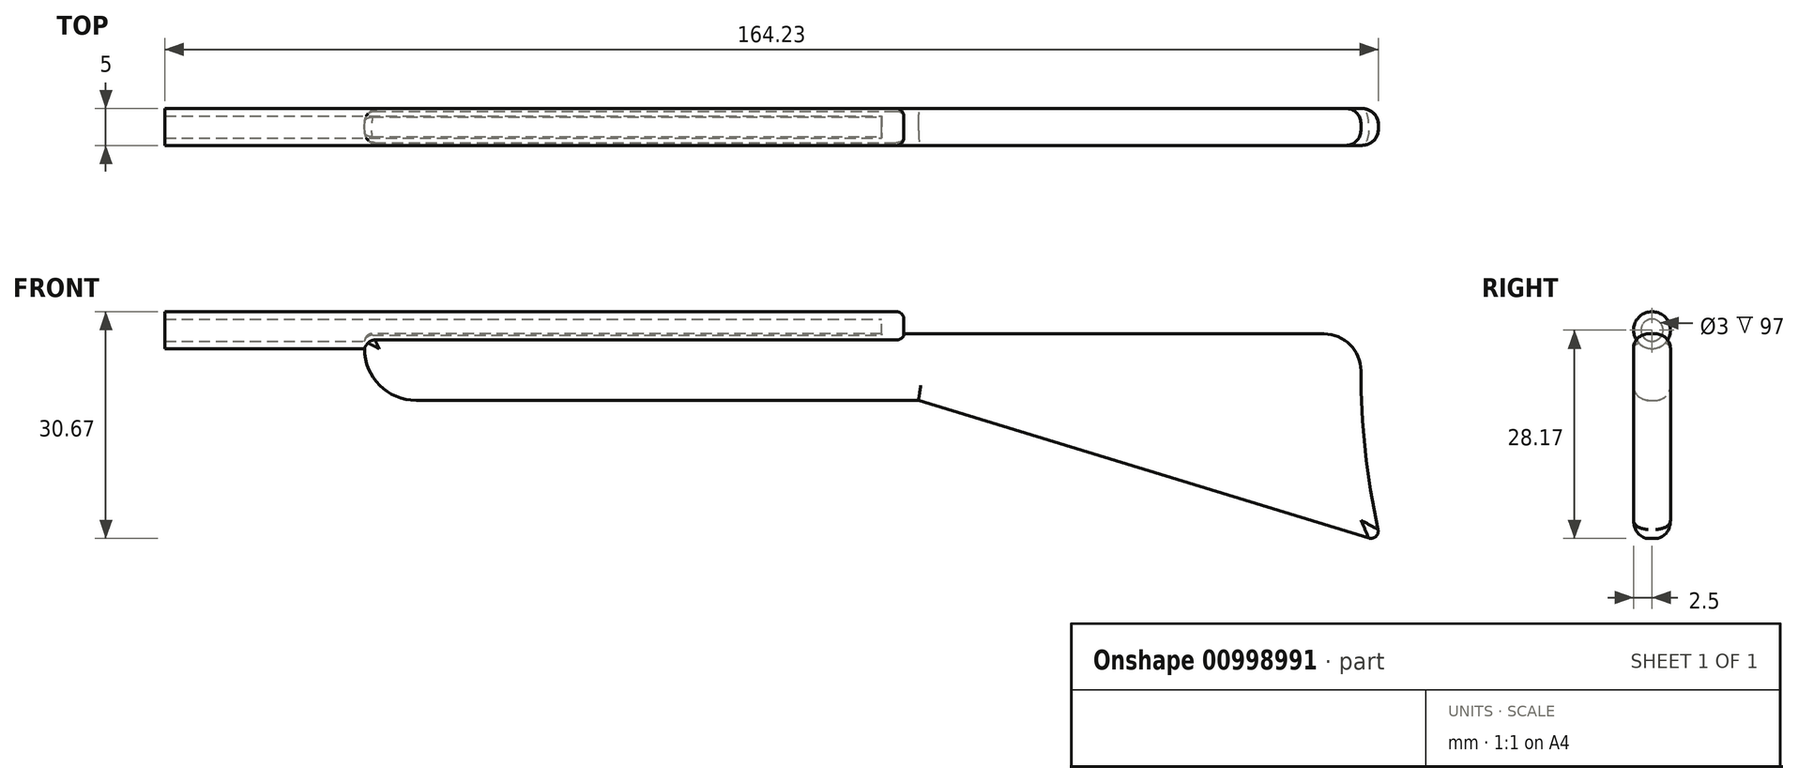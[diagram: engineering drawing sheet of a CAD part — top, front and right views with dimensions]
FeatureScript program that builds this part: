
annotation { "Feature Type Name" : "Feature", "Feature Type Description" : "" }
export const myFeature = defineFeature(function(context is Context, id is Id, definition is map)
    precondition{}
    {
        {
            var Q0;
            Q0=qCreatedBy(makeId("Front.planeOp"),FACE);
            var sketch = newSketch(context, id + "F0", { "sketchPlane" : qUnion([Q0])});
            skLineSegment(sketch, "E0.bottom", {"start": v(-100, 5) * mm, "end": v(0, 5) * mm});
            skLineSegment(sketch, "E0.top", {"start": v(-100, 0) * mm, "end": v(0, 0) * mm});
            skLineSegment(sketch, "E0.left", {"start": v(-100, 5) * mm, "end": v(-100, 0) * mm});
            skLineSegment(sketch, "E0.right", {"start": v(0, 5) * mm, "end": v(0, 0) * mm});
            skArc(sketch, "E1", {"start": v(-73, 0) * mm, "mid": v(-70.95, -4.95) * mm, "end": v(-66, -7) * mm});
            skLineSegment(sketch, "E2", {"start": v(-66, -7) * mm, "end": v(2, -7) * mm});
            skLineSegment(sketch, "E3", {"start": v(2, -7) * mm, "end": v(64.59, -26.14) * mm});
            skArc(sketch, "E4", {"start": v(62, 2) * mm, "mid": v(62.3, -12.16) * mm, "end": v(64.59, -26.14) * mm});
            skPoint(sketch, "E5.endSnap0", {"position": v(0, 2.5) * mm});
            skLineSegment(sketch, "E6", {"start": v(62, 2) * mm, "end": v(-73, 2) * mm});
            skLineSegment(sketch, "E7", {"start": v(-73, 2) * mm, "end": v(-73, 0) * mm});
            skSolve(sketch);
        }
        {
            var Q0;
            Q0=qCreatedBy(makeId("Front.planeOp"),FACE);
            var sketch = newSketch(context, id + "F1", { "sketchPlane" : qUnion([Q0])});
            skArc(sketch, "E8.4", {"start": v(-73, 0) * mm, "mid": v(-70.95, -4.95) * mm, "end": v(-66, -7) * mm});
            skLineSegment(sketch, "E8.5", {"start": v(-66, -7) * mm, "end": v(2, -7) * mm});
            skLineSegment(sketch, "E8.6", {"start": v(2, -7) * mm, "end": v(64.59, -26.14) * mm});
            skArc(sketch, "E8.7", {"start": v(62, 2) * mm, "mid": v(62.3, -12.16) * mm, "end": v(64.59, -26.14) * mm});
            skLineSegment(sketch, "E8.9", {"start": v(62, 2) * mm, "end": v(-73, 2) * mm});
            skLineSegment(sketch, "E8.10", {"start": v(-73, 2) * mm, "end": v(-73, 0) * mm});
            skSolve(sketch);
        }
        {
            var Q0;
            Q0 = qSketchRegion(id + "F1", true);
            extrude(context, id + "F2", {"entities" : qUnion([Q0]), "endBound" : BoundingType.SYMMETRIC, "depth" : 5 * mm, "offsetDistance" : 25 * mm});
        }
        {
            var Q0;
            Q0=makeQuery(id+"F2.opExtrude","CAP_FACE",FACE,{"disambiguationData":[OSD([sQuery(id+"F1.wireOp",EDGE,"E8.4"),sQuery(id+"F1.wireOp",EDGE,"E8.5"),sQuery(id+"F1.wireOp",EDGE,"E8.6"),sQuery(id+"F1.wireOp",EDGE,"E8.7"),sQuery(id+"F1.wireOp",EDGE,"E8.9"),sQuery(id+"F1.wireOp",EDGE,"E8.10")])],"isStart":false});
            var Q1;
            Q1=makeQuery(id+"F2.opExtrude","CAP_FACE",FACE,{"disambiguationData":[OSD([sQuery(id+"F1.wireOp",EDGE,"E8.4"),sQuery(id+"F1.wireOp",EDGE,"E8.5"),sQuery(id+"F1.wireOp",EDGE,"E8.6"),sQuery(id+"F1.wireOp",EDGE,"E8.7"),sQuery(id+"F1.wireOp",EDGE,"E8.9"),sQuery(id+"F1.wireOp",EDGE,"E8.10")])],"isStart":true});
            fillet(context, id + "F3", {"entities" : qUnion([Q0, Q1]), "radius" : 2 * mm, "tangentPropagation" : true, "allowEdgeOverflow" : false});
        }
        {
            var Q0;
            Q0=makeQuery(id+"F2.opExtrude","SWEPT_EDGE",EDGE,{"disambiguationData":[OSD([sQuery(id+"F1.wireOp",EDGE,"E8.7"),sQuery(id+"F1.wireOp",EDGE,"E8.9")])]});
            var Q1;
            Q1=makeQuery(id+"F3.opFillet","BLEND_EDGE",EDGE,{"blendedFrom":[makeQuery(id+"F2.opExtrude","CAP_EDGE",EDGE,{"disambiguationData":[OSD([sQuery(id+"F1.wireOp",EDGE,"E8.7")])],"isStart":false}),makeQuery(id+"F2.opExtrude","CAP_EDGE",EDGE,{"disambiguationData":[OSD([sQuery(id+"F1.wireOp",EDGE,"E8.9")])],"isStart":false})],"blendedInto":[]});
            var Q2;
            Q2=makeQuery(id+"F3.opFillet","BLEND_EDGE",EDGE,{"blendedFrom":[makeQuery(id+"F2.opExtrude","CAP_EDGE",EDGE,{"disambiguationData":[OSD([sQuery(id+"F1.wireOp",EDGE,"E8.7")])],"isStart":true}),makeQuery(id+"F2.opExtrude","CAP_EDGE",EDGE,{"disambiguationData":[OSD([sQuery(id+"F1.wireOp",EDGE,"E8.9")])],"isStart":true})],"blendedInto":[]});
            fillet(context, id + "F4", {"entities" : qUnion([Q0, Q1, Q2]), "radius" : 5 * mm, "tangentPropagation" : true, "allowEdgeOverflow" : false});
        }
        {
            var Q0;
            Q0=makeQuery(id+"F2.opExtrude","SWEPT_EDGE",EDGE,{"disambiguationData":[OSD([sQuery(id+"F1.wireOp",EDGE,"E8.6"),sQuery(id+"F1.wireOp",EDGE,"E8.7")])]});
            var Q1;
            Q1=makeQuery(id+"F3.opFillet","BLEND_EDGE",EDGE,{"blendedFrom":[makeQuery(id+"F2.opExtrude","CAP_EDGE",EDGE,{"disambiguationData":[OSD([sQuery(id+"F1.wireOp",EDGE,"E8.6")])],"isStart":true}),makeQuery(id+"F2.opExtrude","CAP_EDGE",EDGE,{"disambiguationData":[OSD([sQuery(id+"F1.wireOp",EDGE,"E8.7")])],"isStart":true})],"blendedInto":[]});
            var Q2;
            Q2=makeQuery(id+"F3.opFillet","BLEND_EDGE",EDGE,{"blendedFrom":[makeQuery(id+"F2.opExtrude","CAP_EDGE",EDGE,{"disambiguationData":[OSD([sQuery(id+"F1.wireOp",EDGE,"E8.6")])],"isStart":false}),makeQuery(id+"F2.opExtrude","CAP_EDGE",EDGE,{"disambiguationData":[OSD([sQuery(id+"F1.wireOp",EDGE,"E8.7")])],"isStart":false})],"blendedInto":[]});
            var Q3;
            Q3=makeQuery(id+"F3.opFillet","BLEND_EDGE",EDGE,{"blendedFrom":[makeQuery(id+"F2.opExtrude","CAP_EDGE",EDGE,{"disambiguationData":[OSD([sQuery(id+"F1.wireOp",EDGE,"E8.4")])],"isStart":true}),makeQuery(id+"F2.opExtrude","CAP_EDGE",EDGE,{"disambiguationData":[OSD([sQuery(id+"F1.wireOp",EDGE,"E8.10")])],"isStart":true})],"blendedInto":[]});
            var Q4;
            Q4=makeQuery(id+"F2.opExtrude","SWEPT_EDGE",EDGE,{"disambiguationData":[OSD([sQuery(id+"F1.wireOp",EDGE,"E8.4"),sQuery(id+"F1.wireOp",EDGE,"E8.10")])]});
            var Q5;
            Q5=makeQuery(id+"F3.opFillet","BLEND_EDGE",EDGE,{"blendedFrom":[makeQuery(id+"F2.opExtrude","CAP_EDGE",EDGE,{"disambiguationData":[OSD([sQuery(id+"F1.wireOp",EDGE,"E8.4")])],"isStart":false}),makeQuery(id+"F2.opExtrude","CAP_EDGE",EDGE,{"disambiguationData":[OSD([sQuery(id+"F1.wireOp",EDGE,"E8.10")])],"isStart":false})],"blendedInto":[]});
            var Q6;
            Q6=makeQuery(id+"F3.opFillet","BLEND_EDGE",EDGE,{"blendedFrom":[makeQuery(id+"F2.opExtrude","CAP_EDGE",EDGE,{"disambiguationData":[OSD([sQuery(id+"F1.wireOp",EDGE,"E8.9")])],"isStart":true}),makeQuery(id+"F2.opExtrude","CAP_EDGE",EDGE,{"disambiguationData":[OSD([sQuery(id+"F1.wireOp",EDGE,"E8.10")])],"isStart":true})],"blendedInto":[]});
            var Q7;
            Q7=makeQuery(id+"F3.opFillet","BLEND_EDGE",EDGE,{"blendedFrom":[makeQuery(id+"F2.opExtrude","CAP_EDGE",EDGE,{"disambiguationData":[OSD([sQuery(id+"F1.wireOp",EDGE,"E8.9")])],"isStart":false}),makeQuery(id+"F2.opExtrude","CAP_EDGE",EDGE,{"disambiguationData":[OSD([sQuery(id+"F1.wireOp",EDGE,"E8.10")])],"isStart":false})],"blendedInto":[]});
            var Q8;
            Q8=makeQuery(id+"F2.opExtrude","SWEPT_EDGE",EDGE,{"disambiguationData":[OSD([sQuery(id+"F1.wireOp",EDGE,"E8.9"),sQuery(id+"F1.wireOp",EDGE,"E8.10")])]});
            var Q9;
            {var subQ0=sQuery(id+"F1.wireOp",EDGE,"E8.10");Q9=makeQuery(id+"F3.opFillet","BLEND_EDGE",EDGE,{"blendedFrom":[makeQuery(id+"F2.opExtrude","CAP_EDGE",EDGE,{"disambiguationData":[OSD([subQ0])],"isStart":true}),makeQuery(id+"F2.opExtrude","SWEPT_FACE",FACE,{"disambiguationData":[OSD([subQ0])]})],"blendedInto":[makeQuery(id+"F2.opExtrude","SWEPT_FACE",FACE,{"disambiguationData":[OSD([subQ0])]})]});}
            var Q10;
            {var subQ0=sQuery(id+"F1.wireOp",EDGE,"E8.10");Q10=makeQuery(id+"F3.opFillet","BLEND_EDGE",EDGE,{"blendedFrom":[makeQuery(id+"F2.opExtrude","CAP_EDGE",EDGE,{"disambiguationData":[OSD([subQ0])],"isStart":false}),makeQuery(id+"F2.opExtrude","SWEPT_FACE",FACE,{"disambiguationData":[OSD([subQ0])]})],"blendedInto":[makeQuery(id+"F2.opExtrude","SWEPT_FACE",FACE,{"disambiguationData":[OSD([subQ0])]})]});}
            fillet(context, id + "F5", {"entities" : qUnion([Q0, Q1, Q2, Q3, Q4, Q5, Q6, Q7, Q8, Q9, Q10]), "radius" : 1 * mm, "tangentPropagation" : true, "allowEdgeOverflow" : false});
        }
        {
            var Q0;
            Q0=qCreatedBy(makeId("Front.planeOp"),FACE);
            var sketch = newSketch(context, id + "F6", { "sketchPlane" : qUnion([Q0])});
            skLineSegment(sketch, "E9.0", {"start": v(-100, 5) * mm, "end": v(0, 5) * mm});
            skLineSegment(sketch, "E10", {"start": v(-100, 5) * mm, "end": v(-100, 4) * mm});
            skLineSegment(sketch, "E11", {"start": v(-100, 4) * mm, "end": v(-3, 4) * mm});
            skLineSegment(sketch, "E12", {"start": v(-3, 4) * mm, "end": v(-3, 2.5) * mm});
            skLineSegment(sketch, "E13", {"start": v(-3, 2.5) * mm, "end": v(0, 2.5) * mm});
            skLineSegment(sketch, "E14", {"start": v(0, 5) * mm, "end": v(0, 2.5) * mm});
            skLineSegment(sketch, "E15", {"start": v(-3, 2.5) * mm, "end": v(-78.65, 2.5) * mm, "construction": true});
            skSolve(sketch);
        }
        {
            var Q0;
            Q0 = qSketchRegion(id + "F6", true);
            var Q1;
            Q1=sQuery(id+"F6.wireOp",EDGE,"E15");
            revolve(context, id + "F7", {"operationType" : NewBodyOperationType.ADD, "surfaceOperationType" : NewSurfaceOperationType.NEW, "entities" : qUnion([Q0]), "axis" : qUnion([Q1]), "revolveType" : RevolveType.FULL});
        }
        {
            var Q0;
            Q0=makeQuery(id+"F7.opRevolve","SWEPT_EDGE",EDGE,{"disambiguationData":[OSD([sQuery(id+"F6.wireOp",EDGE,"E9.0"),sQuery(id+"F6.wireOp",EDGE,"E14")])]});
            fillet(context, id + "F8", {"entities" : qUnion([Q0]), "radius" : 1 * mm, "tangentPropagation" : true, "allowEdgeOverflow" : false});
        }
    });
